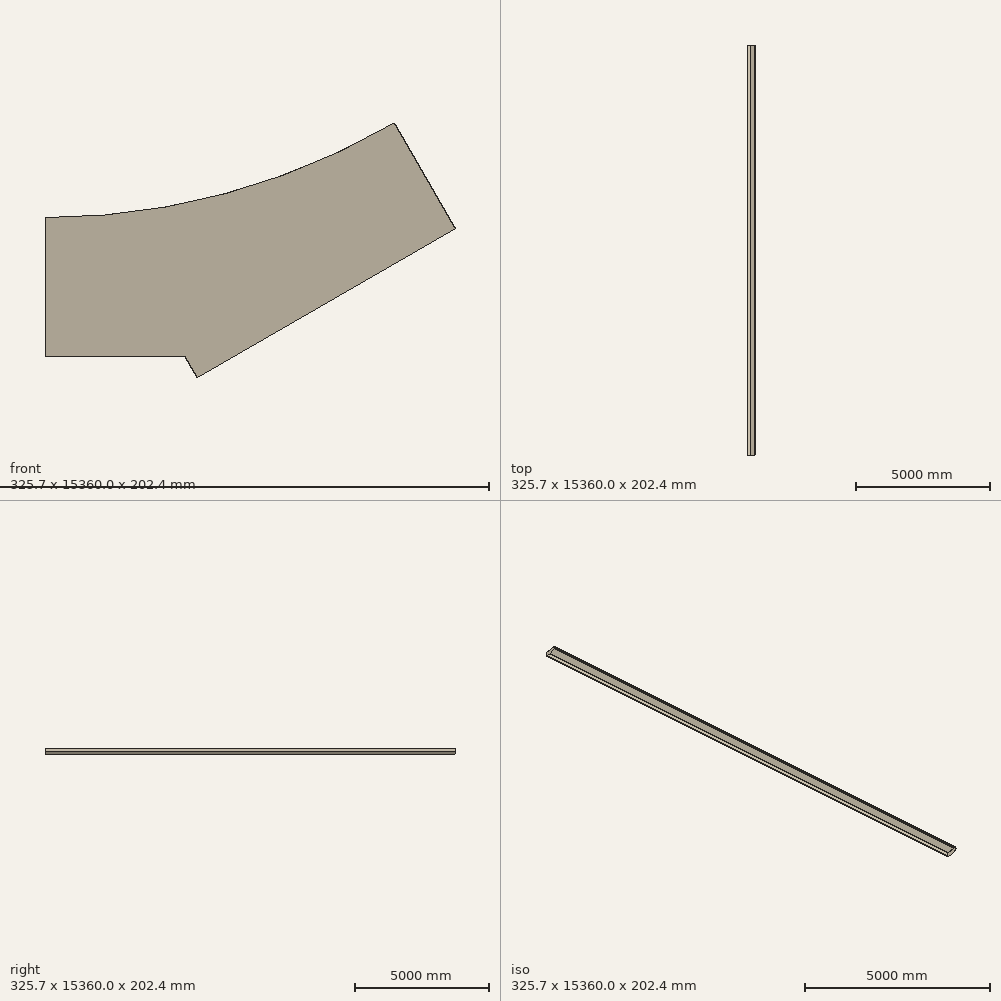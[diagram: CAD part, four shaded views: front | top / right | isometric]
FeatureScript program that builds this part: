
annotation { "Feature Type Name" : "Feature", "Feature Type Description" : "" }
export const myFeature = defineFeature(function(context is Context, id is Id, definition is map)
    precondition{}
    {
        {
            var Q0;
            Q0=qCreatedBy(makeId("Front.planeOp"),FACE);
            var sketch = newSketch(context, id + "F0", { "sketchPlane" : qUnion([Q0])});
            skLineSegment(sketch, "E0", {"start": v(0, 6.36) * mm, "end": v(0, -658.8) * mm});
            skLineSegment(sketch, "E1", {"start": v(0, -658.8) * mm, "end": v(110.6, -658.8) * mm});
            skLineSegment(sketch, "E2", {"start": v(110.6, -658.8) * mm, "end": v(120.6, -676.12) * mm});
            skLineSegment(sketch, "E3", {"start": v(120.6, -676.12) * mm, "end": v(325.67, -557.72) * mm});
            skLineSegment(sketch, "E4", {"start": v(325.67, -557.72) * mm, "end": v(0, 6.36) * mm});
            skSolve(sketch);
        }
        {
            var Q0;
            Q0 = qSketchRegion(id + "F0", true);
            extrude(context, id + "F1", {"entities" : qUnion([Q0]), "oppositeDirection" : true, "depth" : 15880 * mm});
        }
        {
            var Q0;
            Q0=qCreatedBy(makeId("Top.planeOp"),FACE);
            var sketch = newSketch(context, id + "F2", { "sketchPlane" : qUnion([Q0])});
            skLineSegment(sketch, "E5.bottom", {"start": v(0, 520) * mm, "end": v(325.67, 520) * mm});
            skLineSegment(sketch, "E5.top", {"start": v(0, 0) * mm, "end": v(325.67, 0) * mm});
            skLineSegment(sketch, "E5.left", {"start": v(0, 520) * mm, "end": v(0, 0) * mm});
            skLineSegment(sketch, "E5.right", {"start": v(325.67, 520) * mm, "end": v(325.67, 0) * mm});
            skSolve(sketch);
        }
        {
            var Q0;
            Q0 = qSketchRegion(id + "F2", true);
            extrude(context, id + "F3", {"entities" : qUnion([Q0]), "operationType" : NewBodyOperationType.REMOVE, "depth" : 3000 * mm, "hasSecondDirection" : true, "secondDirectionOppositeDirection" : true, "secondDirectionDepth" : 3000 * mm});
        }
        {
            var Q0;
            Q0=makeQuery(id+"F3.boolean.opBoolean","COPY",FACE,{"derivedFrom":makeQuery(id+"F3.opExtrude","SWEPT_FACE",FACE,{"disambiguationData":[OSD([sQuery(id+"F2.wireOp",EDGE,"E5.bottom")])]})});
            cPlane(context, id + "F4", {"entities" : qUnion([Q0]), "cplaneType" : CPlaneType.OFFSET, "offset" : 12 * mm, "oppositeDirection" : true, "width" : 150 * mm, "height" : 150 * mm});
        }
        {
            var Q0;
            Q0=qCreatedBy(id+"F4.planeOp",FACE);
            var sketch = newSketch(context, id + "F5", { "sketchPlane" : qUnion([Q0])});
            skLineSegment(sketch, "E6", {"start": v(0, -648.8) * mm, "end": v(127.92, -648.8) * mm});
            skLineSegment(sketch, "E7", {"start": v(127.92, -648.8) * mm, "end": v(305.28, -546.4) * mm});
            skLineSegment(sketch, "E8", {"start": v(305.28, -546.4) * mm, "end": v(0, -17.64) * mm});
            skLineSegment(sketch, "E9", {"start": v(0, -17.64) * mm, "end": v(0, -648.8) * mm});
            skSolve(sketch);
        }
        {
            var Q0;
            Q0 = qSketchRegion(id + "F5", true);
            extrude(context, id + "F6", {"entities" : qUnion([Q0]), "operationType" : NewBodyOperationType.REMOVE, "oppositeDirection" : true, "depth" : 15336 * mm});
        }
        {
            var Q0;
            Q0=makeQuery(id+"F3.boolean.opBoolean","COPY",FACE,{"derivedFrom":makeQuery(id+"F3.opExtrude","SWEPT_FACE",FACE,{"disambiguationData":[OSD([sQuery(id+"F2.wireOp",EDGE,"E5.bottom")])]})});
            var sketch = newSketch(context, id + "F7", { "sketchPlane" : qUnion([Q0])});
            skCircle(sketch, "E10", {"center": v(0, 0) * mm, "radius": 548.8 * mm});
            skSolve(sketch);
        }
        {
            var Q0;
            Q0 = qSketchRegion(id + "F7", true);
            extrude(context, id + "F8", {"entities" : qUnion([Q0]), "operationType" : NewBodyOperationType.REMOVE, "oppositeDirection" : true, "depth" : 15360 * mm});
        }
    });
